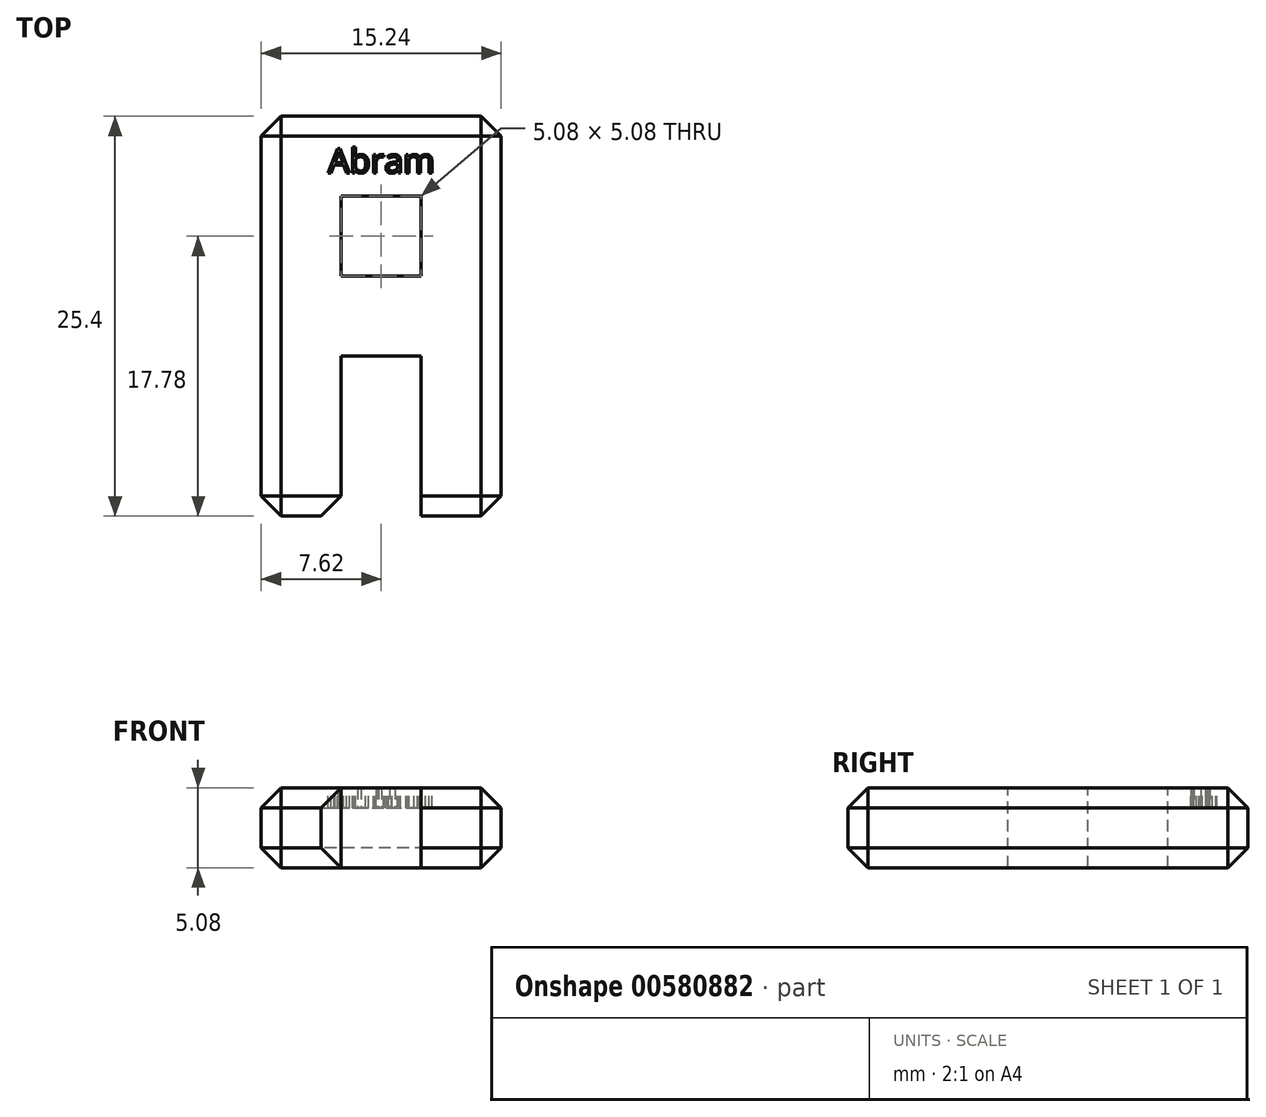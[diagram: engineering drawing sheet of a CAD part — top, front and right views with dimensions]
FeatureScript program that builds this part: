
annotation { "Feature Type Name" : "Feature", "Feature Type Description" : "" }
export const myFeature = defineFeature(function(context is Context, id is Id, definition is map)
    precondition{}
    {
        {
            var Q0;
            Q0=qCreatedBy(makeId("Top.planeOp"),FACE);
            var sketch = newSketch(context, id + "F0", { "sketchPlane" : qUnion([Q0])});
            skLineSegment(sketch, "E0.bottom", {"start": v(7.62, 12.7) * mm, "end": v(-7.62, 12.7) * mm});
            skLineSegment(sketch, "E0.top", {"start": v(7.62, -12.7) * mm, "end": v(-7.62, -12.7) * mm});
            skLineSegment(sketch, "E0.left", {"start": v(7.62, 12.7) * mm, "end": v(7.62, -12.7) * mm});
            skLineSegment(sketch, "E0.right", {"start": v(-7.62, 12.7) * mm, "end": v(-7.62, -12.7) * mm});
            skPoint(sketch, "E0.middle", {"position": v(0, 0) * mm});
            skSolve(sketch);
        }
        {
            var Q0;
            Q0=makeQuery(id+"F0.imprint","IMPRINT",FACE,{"disambiguationData":[TD([[makeQuery(id+"F0.imprint","IMPRINT",EDGE,{"derivedFrom":sQuery(id+"F0.wireOp",EDGE,"E0.bottom")}),1.0]])]});
            extrude(context, id + "F1", {"entities" : qUnion([Q0]), "depth" : 5.08 * mm, "offsetDistance" : 25.4 * mm});
        }
        {
            var Q0;
            Q0=makeQuery(id+"F1.opExtrude","CAP_FACE",FACE,{"disambiguationData":[OSD([sQuery(id+"F0.wireOp",EDGE,"E0.bottom"),sQuery(id+"F0.wireOp",EDGE,"E0.top"),sQuery(id+"F0.wireOp",EDGE,"E0.left"),sQuery(id+"F0.wireOp",EDGE,"E0.right")])],"isStart":false});
            var sketch = newSketch(context, id + "F2", { "sketchPlane" : qUnion([Q0])});
            skLineSegment(sketch, "E1.bottom", {"start": v(-2.54, -12.7) * mm, "end": v(2.54, -12.7) * mm});
            skLineSegment(sketch, "E1.top", {"start": v(-2.54, -2.54) * mm, "end": v(2.54, -2.54) * mm});
            skLineSegment(sketch, "E1.left", {"start": v(-2.54, -12.7) * mm, "end": v(-2.54, -2.54) * mm});
            skLineSegment(sketch, "E1.right", {"start": v(2.54, -12.7) * mm, "end": v(2.54, -2.54) * mm});
            skLineSegment(sketch, "E2.bottom", {"start": v(-2.54, 7.62) * mm, "end": v(2.54, 7.62) * mm});
            skLineSegment(sketch, "E2.top", {"start": v(-2.54, 2.54) * mm, "end": v(2.54, 2.54) * mm});
            skLineSegment(sketch, "E2.left", {"start": v(-2.54, 7.62) * mm, "end": v(-2.54, 2.54) * mm});
            skLineSegment(sketch, "E2.right", {"start": v(2.54, 7.62) * mm, "end": v(2.54, 2.54) * mm});
            skSolve(sketch);
        }
        {
            var Q0;
            Q0=makeQuery(id+"F2.imprint","IMPRINT",FACE,{"disambiguationData":[TD([[makeQuery(id+"F2.imprint","IMPRINT",EDGE,{"derivedFrom":sQuery(id+"F2.wireOp",EDGE,"E2.bottom")}),-1.0]])]});
            var Q1;
            Q1=makeQuery(id+"F2.imprint","IMPRINT",FACE,{"disambiguationData":[TD([[makeQuery(id+"F2.imprint","IMPRINT",EDGE,{"derivedFrom":sQuery(id+"F2.wireOp",EDGE,"E1.bottom")}),-1.0]])]});
            extrude(context, id + "F3", {"entities" : qUnion([Q0, Q1]), "operationType" : NewBodyOperationType.REMOVE, "oppositeDirection" : true, "depth" : 5.08 * mm, "offsetDistance" : 25.4 * mm});
        }
        {
            var Q0;
            Q0=makeQuery(id+"F1.opExtrude","CAP_FACE",FACE,{"disambiguationData":[OSD([sQuery(id+"F0.wireOp",EDGE,"E0.bottom"),sQuery(id+"F0.wireOp",EDGE,"E0.top"),sQuery(id+"F0.wireOp",EDGE,"E0.left"),sQuery(id+"F0.wireOp",EDGE,"E0.right")])],"isStart":false});
            var sketch = newSketch(context, id + "F4", { "sketchPlane" : qUnion([Q0])});
            skText(sketch, "E3", { "text": "Abram", "fontName": "OpenSans-Regular.ttf"});
            skPoint(sketch, "E4", {"position": v(0, 12.7) * mm});
            const initialGuessF4  = {"E3": [-0.00337, 0.0091, 1, 0, 0.00155]};
            skSetInitialGuess(sketch, initialGuessF4);
            skSolve(sketch);
        }
        {
            var Q0;
            Q0=makeQuery(id+"F3.boolean.opBoolean","COPY",EDGE,{"derivedFrom":makeQuery(id+"F3.opExtrude","CAP_EDGE",EDGE,{"disambiguationData":[OSD([sQuery(id+"F2.wireOp",EDGE,"E2.top")])],"isStart":true})});
            var Q1;
            Q1=makeQuery(id+"F3.boolean.opBoolean","COPY",EDGE,{"derivedFrom":makeQuery(id+"F3.opExtrude","CAP_EDGE",EDGE,{"disambiguationData":[OSD([sQuery(id+"F2.wireOp",EDGE,"E2.left")])],"isStart":true})});
            var Q2;
            Q2=makeQuery(id+"F3.boolean.opBoolean","COPY",EDGE,{"derivedFrom":makeQuery(id+"F3.opExtrude","CAP_EDGE",EDGE,{"disambiguationData":[OSD([sQuery(id+"F2.wireOp",EDGE,"E2.right")])],"isStart":true})});
            var Q3;
            Q3=makeQuery(id+"F3.boolean.opBoolean","COPY",EDGE,{"derivedFrom":makeQuery(id+"F3.opExtrude","CAP_EDGE",EDGE,{"disambiguationData":[OSD([sQuery(id+"F2.wireOp",EDGE,"E2.bottom")])],"isStart":true})});
            var Q4;
            Q4=makeQuery(id+"F3.boolean.opBoolean","COPY",EDGE,{"derivedFrom":makeQuery(id+"F3.opExtrude","CAP_EDGE",EDGE,{"disambiguationData":[OSD([sQuery(id+"F2.wireOp",EDGE,"E2.top")])],"isStart":false})});
            var Q5;
            Q5=makeQuery(id+"F3.boolean.opBoolean","COPY",EDGE,{"derivedFrom":makeQuery(id+"F3.opExtrude","CAP_EDGE",EDGE,{"disambiguationData":[OSD([sQuery(id+"F2.wireOp",EDGE,"E2.right")])],"isStart":false})});
            var Q6;
            Q6=makeQuery(id+"F3.boolean.opBoolean","COPY",EDGE,{"derivedFrom":makeQuery(id+"F3.opExtrude","CAP_EDGE",EDGE,{"disambiguationData":[OSD([sQuery(id+"F2.wireOp",EDGE,"E2.bottom")])],"isStart":false})});
            var Q7;
            Q7=makeQuery(id+"F3.boolean.opBoolean","COPY",EDGE,{"derivedFrom":makeQuery(id+"F3.opExtrude","CAP_EDGE",EDGE,{"disambiguationData":[OSD([sQuery(id+"F2.wireOp",EDGE,"E2.left")])],"isStart":false})});
            var Q8;
            Q8=makeQuery(id+"F1.opExtrude","CAP_EDGE",EDGE,{"disambiguationData":[OSD([sQuery(id+"F0.wireOp",EDGE,"E0.bottom")])],"isStart":true});
            var Q9;
            Q9=makeQuery(id+"F1.opExtrude","CAP_EDGE",EDGE,{"disambiguationData":[OSD([sQuery(id+"F0.wireOp",EDGE,"E0.bottom")])],"isStart":false});
            var Q10;
            Q10=makeQuery(id+"F3.boolean.opBoolean","COPY",EDGE,{"derivedFrom":makeQuery(id+"F3.opExtrude","CAP_EDGE",EDGE,{"disambiguationData":[OSD([sQuery(id+"F2.wireOp",EDGE,"E1.top")])],"isStart":false})});
            var Q11;
            Q11=makeQuery(id+"F3.boolean.opBoolean","COPY",EDGE,{"derivedFrom":makeQuery(id+"F3.opExtrude","CAP_EDGE",EDGE,{"disambiguationData":[OSD([sQuery(id+"F2.wireOp",EDGE,"E1.top")])],"isStart":true})});
            var Q12;
            {var subQ0=sQuery(id+"F0.wireOp",EDGE,"E0.right");var subQ1=sQuery(id+"F0.wireOp",EDGE,"E0.top");Q12=makeQuery(id+"F3.boolean.opBoolean","SPLIT",EDGE,{"disambiguationData":[TD([makeQuery(id+"F1.opExtrude","SWEPT_FACE",FACE,{"disambiguationData":[OSD([subQ0])]})])],"derivedFrom":makeQuery(id+"F1.opExtrude","CAP_EDGE",EDGE,{"disambiguationData":[OSD([subQ1])],"isStart":false})});}
            var Q13;
            {var subQ0=sQuery(id+"F0.wireOp",EDGE,"E0.left");var subQ1=sQuery(id+"F0.wireOp",EDGE,"E0.top");Q13=makeQuery(id+"F3.boolean.opBoolean","SPLIT",EDGE,{"disambiguationData":[TD([makeQuery(id+"F1.opExtrude","SWEPT_FACE",FACE,{"disambiguationData":[OSD([subQ0])]})])],"derivedFrom":makeQuery(id+"F1.opExtrude","CAP_EDGE",EDGE,{"disambiguationData":[OSD([subQ1])],"isStart":true})});}
            var Q14;
            {var subQ0=sQuery(id+"F0.wireOp",EDGE,"E0.right");var subQ1=sQuery(id+"F0.wireOp",EDGE,"E0.top");Q14=makeQuery(id+"F3.boolean.opBoolean","SPLIT",EDGE,{"disambiguationData":[TD([makeQuery(id+"F1.opExtrude","SWEPT_FACE",FACE,{"disambiguationData":[OSD([subQ0])]})])],"derivedFrom":makeQuery(id+"F1.opExtrude","CAP_EDGE",EDGE,{"disambiguationData":[OSD([subQ1])],"isStart":true})});}
            var Q15;
            {var subQ0=sQuery(id+"F0.wireOp",EDGE,"E0.left");var subQ1=sQuery(id+"F0.wireOp",EDGE,"E0.top");Q15=makeQuery(id+"F3.boolean.opBoolean","SPLIT",EDGE,{"disambiguationData":[TD([makeQuery(id+"F1.opExtrude","SWEPT_FACE",FACE,{"disambiguationData":[OSD([subQ0])]})])],"derivedFrom":makeQuery(id+"F1.opExtrude","CAP_EDGE",EDGE,{"disambiguationData":[OSD([subQ1])],"isStart":false})});}
            var Q16;
            Q16=makeQuery(id+"F1.opExtrude","CAP_EDGE",EDGE,{"disambiguationData":[OSD([sQuery(id+"F0.wireOp",EDGE,"E0.left")])],"isStart":true});
            var Q17;
            Q17=makeQuery(id+"F1.opExtrude","CAP_EDGE",EDGE,{"disambiguationData":[OSD([sQuery(id+"F0.wireOp",EDGE,"E0.right")])],"isStart":true});
            var Q18;
            Q18=makeQuery(id+"F1.opExtrude","CAP_EDGE",EDGE,{"disambiguationData":[OSD([sQuery(id+"F0.wireOp",EDGE,"E0.left")])],"isStart":false});
            var Q19;
            Q19=makeQuery(id+"F1.opExtrude","CAP_EDGE",EDGE,{"disambiguationData":[OSD([sQuery(id+"F0.wireOp",EDGE,"E0.right")])],"isStart":false});
            var Q20;
            Q20=makeQuery(id+"F3.boolean.opBoolean","COPY",EDGE,{"derivedFrom":makeQuery(id+"F3.opExtrude","CAP_EDGE",EDGE,{"disambiguationData":[OSD([sQuery(id+"F2.wireOp",EDGE,"E1.left")])],"isStart":true})});
            var Q21;
            Q21=makeQuery(id+"F3.boolean.opBoolean","COPY",EDGE,{"derivedFrom":makeQuery(id+"F3.opExtrude","CAP_EDGE",EDGE,{"disambiguationData":[OSD([sQuery(id+"F2.wireOp",EDGE,"E1.right")])],"isStart":true})});
            var Q22;
            Q22=makeQuery(id+"F3.boolean.opBoolean","COPY",EDGE,{"derivedFrom":makeQuery(id+"F3.opExtrude","CAP_EDGE",EDGE,{"disambiguationData":[OSD([sQuery(id+"F2.wireOp",EDGE,"E1.left")])],"isStart":false})});
            var Q23;
            Q23=makeQuery(id+"F3.boolean.opBoolean","COPY",EDGE,{"derivedFrom":makeQuery(id+"F3.opExtrude","CAP_EDGE",EDGE,{"disambiguationData":[OSD([sQuery(id+"F2.wireOp",EDGE,"E1.right")])],"isStart":false})});
            var Q24;
            Q24=makeQuery(id+"F1.opExtrude","SWEPT_EDGE",EDGE,{"disambiguationData":[OSD([sQuery(id+"F0.wireOp",EDGE,"E0.bottom"),sQuery(id+"F0.wireOp",EDGE,"E0.right")])]});
            var Q25;
            Q25=makeQuery(id+"F1.opExtrude","SWEPT_EDGE",EDGE,{"disambiguationData":[OSD([sQuery(id+"F0.wireOp",EDGE,"E0.bottom"),sQuery(id+"F0.wireOp",EDGE,"E0.left")])]});
            var Q26;
            Q26=makeQuery(id+"F1.opExtrude","SWEPT_EDGE",EDGE,{"disambiguationData":[OSD([sQuery(id+"F0.wireOp",EDGE,"E0.top"),sQuery(id+"F0.wireOp",EDGE,"E0.left")])]});
            var Q27;
            Q27=makeQuery(id+"F3.boolean.opBoolean","COPY",EDGE,{"derivedFrom":makeQuery(id+"F3.opExtrude","SWEPT_EDGE",EDGE,{"disambiguationData":[OSD([sQuery(id+"F0.wireOp",EDGE,"E0.top"),sQuery(id+"F2.wireOp",EDGE,"E1.bottom"),sQuery(id+"F2.wireOp",EDGE,"E1.right")])]})});
            var Q28;
            Q28=makeQuery(id+"F3.boolean.opBoolean","COPY",EDGE,{"derivedFrom":makeQuery(id+"F3.opExtrude","SWEPT_EDGE",EDGE,{"disambiguationData":[OSD([sQuery(id+"F0.wireOp",EDGE,"E0.top"),sQuery(id+"F2.wireOp",EDGE,"E1.bottom"),sQuery(id+"F2.wireOp",EDGE,"E1.left")])]})});
            var Q29;
            Q29=makeQuery(id+"F1.opExtrude","SWEPT_EDGE",EDGE,{"disambiguationData":[OSD([sQuery(id+"F0.wireOp",EDGE,"E0.top"),sQuery(id+"F0.wireOp",EDGE,"E0.right")])]});
            chamfer(context, id + "F5", {"entities" : qUnion([Q0, Q1, Q2, Q3, Q4, Q5, Q6, Q7, Q8, Q9, Q10, Q11, Q12, Q13, Q14, Q15, Q16, Q17, Q18, Q19, Q20, Q21, Q22, Q23, Q24, Q25, Q26, Q27, Q28, Q29]), "width" : 1.27 * mm, "tangentPropagation" : true});
        }
        {
            var Q0;
            Q0 = qSketchRegion(id + "F4", true);
            extrude(context, id + "F6", {"entities" : qUnion([Q0]), "operationType" : NewBodyOperationType.REMOVE, "oppositeDirection" : true, "depth" : 1.27 * mm, "offsetDistance" : 25.4 * mm});
        }
    });
